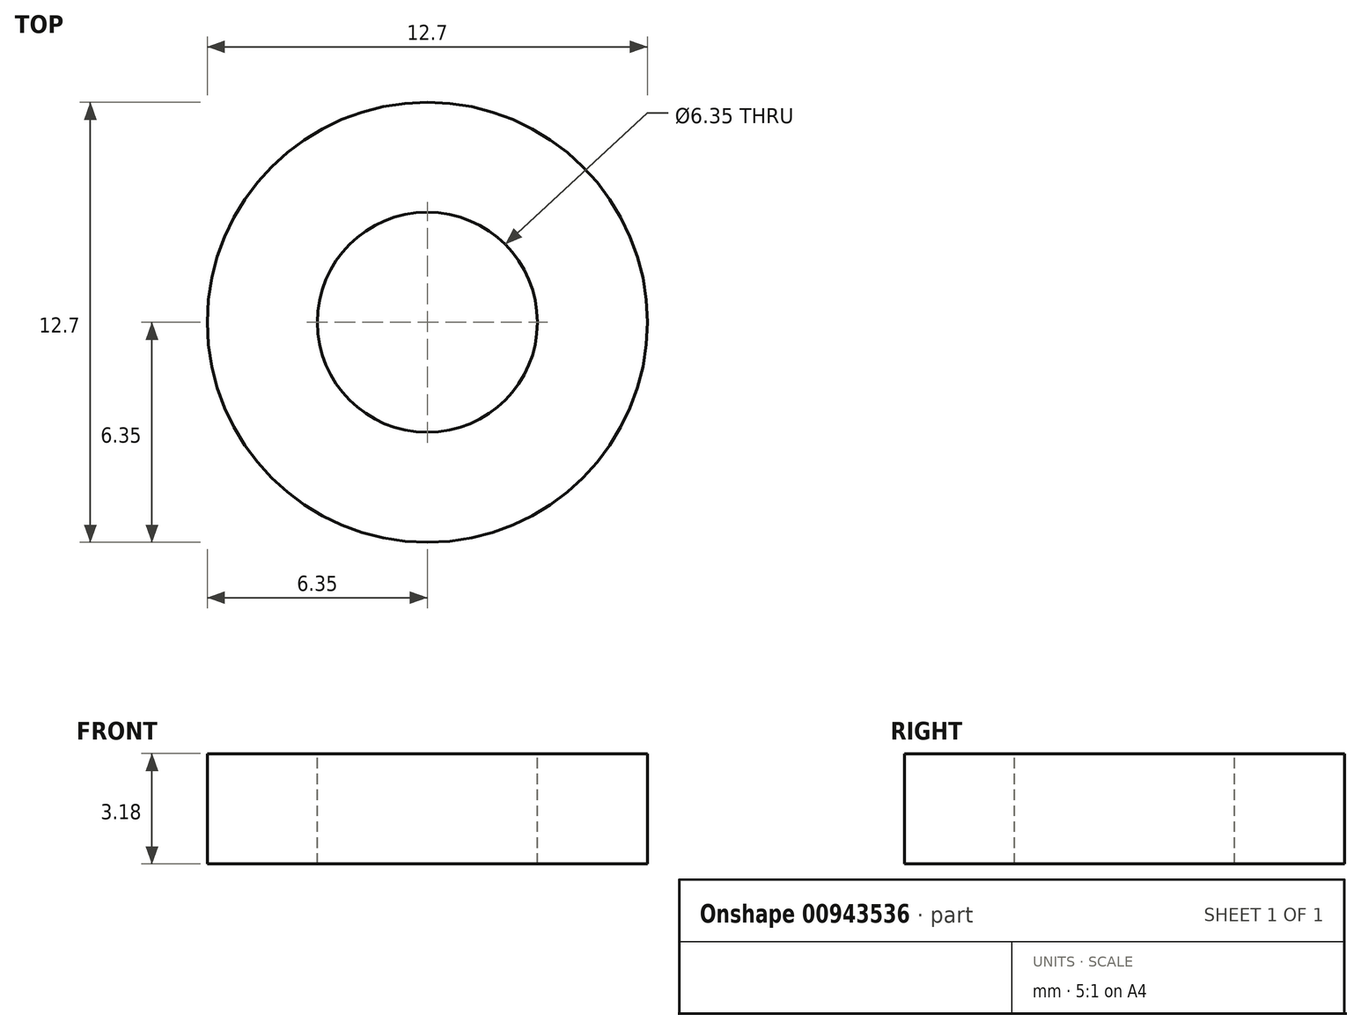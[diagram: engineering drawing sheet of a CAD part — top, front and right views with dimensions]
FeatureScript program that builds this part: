
annotation { "Feature Type Name" : "Feature", "Feature Type Description" : "" }
export const myFeature = defineFeature(function(context is Context, id is Id, definition is map)
    precondition{}
    {
        {
            var Q0;
            Q0=qCreatedBy(makeId("Front.planeOp"),FACE);
            var sketch = newSketch(context, id + "F0", { "sketchPlane" : qUnion([Q0])});
            skLineSegment(sketch, "E0.bottom", {"start": v(3.17, 0) * mm, "end": v(6.35, 0) * mm});
            skLineSegment(sketch, "E0.top", {"start": v(3.17, 3.17) * mm, "end": v(6.35, 3.17) * mm});
            skLineSegment(sketch, "E0.left", {"start": v(3.17, 0) * mm, "end": v(3.17, 3.17) * mm});
            skLineSegment(sketch, "E0.right", {"start": v(6.35, 0) * mm, "end": v(6.35, 3.17) * mm});
            skLineSegment(sketch, "E1", {"start": v(0, 3.17) * mm, "end": v(0, 0) * mm, "construction": true});
            skSolve(sketch);
        }
        {
            var Q0;
            Q0=makeQuery(id+"F0.imprint","IMPRINT",FACE,{"disambiguationData":[TD([[makeQuery(id+"F0.imprint","IMPRINT",EDGE,{"derivedFrom":sQuery(id+"F0.wireOp",EDGE,"E0.bottom")}),1.0]])]});
            var Q1;
            Q1=sQuery(id+"F0.wireOp",EDGE,"E1");
            revolve(context, id + "F1", {"surfaceOperationType" : NewSurfaceOperationType.NEW, "entities" : qUnion([Q0]), "axis" : qUnion([Q1]), "revolveType" : RevolveType.FULL});
        }
    });
